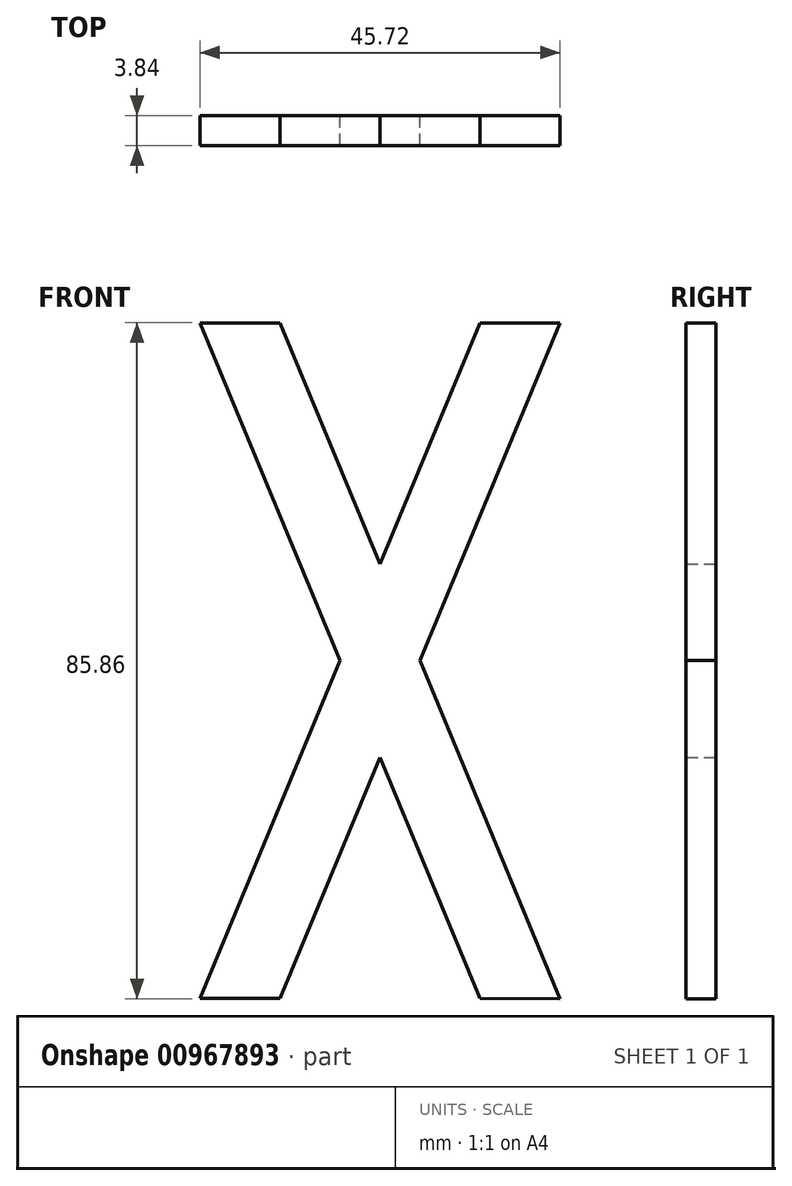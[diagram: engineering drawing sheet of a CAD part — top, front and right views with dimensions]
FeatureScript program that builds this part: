
annotation { "Feature Type Name" : "Feature", "Feature Type Description" : "" }
export const myFeature = defineFeature(function(context is Context, id is Id, definition is map)
    precondition{}
    {
        {
            var Q0;
            Q0=qCreatedBy(makeId("Front.planeOp"),FACE);
            var sketch = newSketch(context, id + "F0", { "sketchPlane" : qUnion([Q0])});
            skLineSegment(sketch, "E0", {"start": v(10.16, 54.42) * mm, "end": v(22.86, 23.76) * mm});
            skPoint(sketch, "E0.endSnap0", {"position": v(22.86, 54.42) * mm});
            skLineSegment(sketch, "E1", {"start": v(22.86, 23.76) * mm, "end": v(35.56, 54.42) * mm});
            skLineSegment(sketch, "E2", {"start": v(10.16, 54.42) * mm, "end": v(0, 54.42) * mm});
            skLineSegment(sketch, "E3", {"start": v(22.86, 23.76) * mm, "end": v(0, -31.43) * mm});
            skLineSegment(sketch, "E4", {"start": v(22.86, 23.76) * mm, "end": v(45.72, -31.44) * mm});
            skLineSegment(sketch, "E5", {"start": v(35.56, 54.42) * mm, "end": v(45.72, 54.42) * mm});
            skLineSegment(sketch, "E6", {"start": v(45.72, 54.42) * mm, "end": v(10.16, -31.43) * mm});
            skLineSegment(sketch, "E7", {"start": v(10.16, -31.43) * mm, "end": v(0, -31.43) * mm});
            skLineSegment(sketch, "E8", {"start": v(0, 54.42) * mm, "end": v(35.56, -31.43) * mm});
            skLineSegment(sketch, "E9", {"start": v(35.56, -31.43) * mm, "end": v(45.72, -31.44) * mm});
            skSolve(sketch);
        }
        {
            var Q0;
            {var subQ0=sQuery(id+"F0.wireOp",EDGE,"E1");Q0=makeQuery(id+"F0.imprint","IMPRINT",FACE,{"disambiguationData":[TD([[makeQuery(id+"F0.imprint","IMPRINT",EDGE,{"derivedFrom":subQ0}),-1.0]])]});}
            var Q1;
            {var subQ0=sQuery(id+"F0.wireOp",EDGE,"E0");Q1=makeQuery(id+"F0.imprint","IMPRINT",FACE,{"disambiguationData":[TD([[makeQuery(id+"F0.imprint","IMPRINT",EDGE,{"derivedFrom":subQ0}),-1.0]])]});}
            var Q2;
            {var subQ0=sQuery(id+"F0.wireOp",EDGE,"E4");var subQ5=sQuery(id+"F0.wireOp",EDGE,"E6");var subQ7=makeQuery(id+"F0.imprint","INTERSECT",VERTEX,{"derivedFrom":[subQ0,subQ5]});Q2=makeQuery(id+"F0.imprint","IMPRINT",FACE,{"disambiguationData":[TD([[makeQuery(id+"F0.imprint","IMPRINT",EDGE,{"disambiguationData":[TD([[subQ7,-1.0]])],"derivedFrom":subQ5}),-1.0]])]});}
            var Q3;
            {var subQ0=sQuery(id+"F0.wireOp",EDGE,"E9");Q3=makeQuery(id+"F0.imprint","IMPRINT",FACE,{"disambiguationData":[TD([[makeQuery(id+"F0.imprint","IMPRINT",EDGE,{"derivedFrom":subQ0}),1.0]])]});}
            var Q4;
            {var subQ0=sQuery(id+"F0.wireOp",EDGE,"E7");Q4=makeQuery(id+"F0.imprint","IMPRINT",FACE,{"disambiguationData":[TD([[makeQuery(id+"F0.imprint","IMPRINT",EDGE,{"derivedFrom":subQ0}),-1.0]])]});}
            extrude(context, id + "F1", {"entities" : qUnion([Q0, Q1, Q2, Q3, Q4]), "depth" : 6.38 * mm, "offsetDistance" : 25.4 * mm});
        }
        {
            var Q0;
            Q0=makeQuery(id+"F1.opExtrude","CAP_FACE",FACE,{"disambiguationData":[OSD([sQuery(id+"F0.wireOp",EDGE,"E0"),sQuery(id+"F0.wireOp",EDGE,"E1"),sQuery(id+"F0.wireOp",EDGE,"E2"),sQuery(id+"F0.wireOp",EDGE,"E3"),sQuery(id+"F0.wireOp",EDGE,"E4"),sQuery(id+"F0.wireOp",EDGE,"E5"),sQuery(id+"F0.wireOp",EDGE,"E6"),sQuery(id+"F0.wireOp",EDGE,"E7"),sQuery(id+"F0.wireOp",EDGE,"E8"),sQuery(id+"F0.wireOp",EDGE,"E9")])],"isStart":false});
            extrude(context, id + "F2", {"entities" : qUnion([Q0]), "operationType" : NewBodyOperationType.REMOVE, "surfaceOperationType" : NewSurfaceOperationType.ADD, "oppositeDirection" : true, "depth" : 2.54 * mm, "offsetDistance" : 25.4 * mm});
        }
    });
